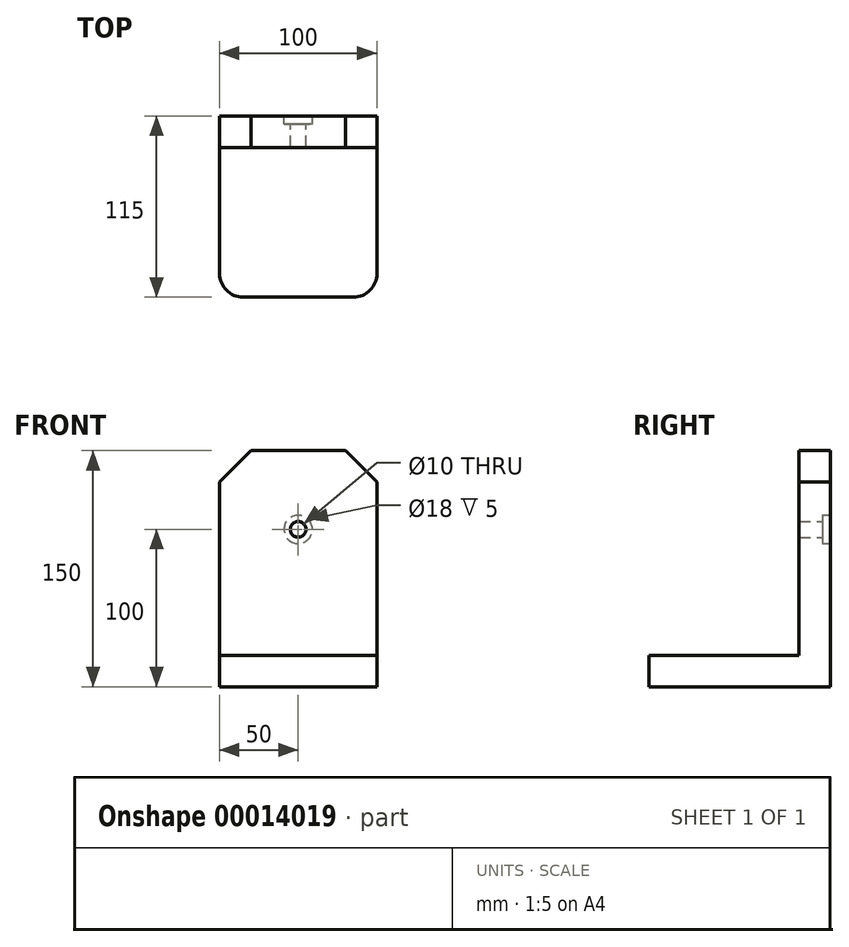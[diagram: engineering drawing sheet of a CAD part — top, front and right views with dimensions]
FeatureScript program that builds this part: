
annotation { "Feature Type Name" : "Feature", "Feature Type Description" : "" }
export const myFeature = defineFeature(function(context is Context, id is Id, definition is map)
    precondition{}
    {
        {
            var Q0;
            Q0=qCreatedBy(makeId("Right.planeOp"),FACE);
            var sketch = newSketch(context, id + "F0", { "sketchPlane" : qUnion([Q0])});
            skLineSegment(sketch, "E0.bottom", {"start": v(0, 0) * mm, "end": v(-20, 0) * mm});
            skLineSegment(sketch, "E0.top", {"start": v(0, 150) * mm, "end": v(-20, 150) * mm});
            skLineSegment(sketch, "E0.left", {"start": v(0, 0) * mm, "end": v(0, 150) * mm});
            skLineSegment(sketch, "E0.right", {"start": v(-20, 0) * mm, "end": v(-20, 150) * mm});
            skLineSegment(sketch, "E1.bottom", {"start": v(0, 20) * mm, "end": v(-115, 20) * mm});
            skLineSegment(sketch, "E1.top", {"start": v(0, 0) * mm, "end": v(-115, 0) * mm});
            skLineSegment(sketch, "E1.left", {"start": v(0, 20) * mm, "end": v(0, 0) * mm});
            skLineSegment(sketch, "E1.right", {"start": v(-115, 20) * mm, "end": v(-115, 0) * mm});
            skSolve(sketch);
        }
        {
            var Q0;
            Q0 = qSketchRegion(id + "F0", true);
            extrude(context, id + "F1", {"entities" : qUnion([Q0]), "endBound" : BoundingType.SYMMETRIC, "depth" : 100 * mm});
        }
        {
            var Q0;
            Q0=makeQuery(id+"F1.opExtrude","SWEPT_FACE",FACE,{"disambiguationData":[OSD([sQuery(id+"F0.wireOp",EDGE,"E0.left"),sQuery(id+"F0.wireOp",EDGE,"E1.left")])]});
            var sketch = newSketch(context, id + "F2", { "sketchPlane" : qUnion([Q0])});
            skPoint(sketch, "E2", {"position": v(0, 100) * mm});
            skSolve(sketch);
        }
        {
            var Q0;
            Q0=sQuery(id+"F2.wireOp",VERTEX,"E2");
            var Q1;
            Q1=makeQuery(id+"F1.opExtrude","SWEPT_BODY",BODY,{"disambiguationData":[OSD([sQuery(id+"F0.wireOp",EDGE,"E0.top"),sQuery(id+"F0.wireOp",EDGE,"E0.left"),sQuery(id+"F0.wireOp",EDGE,"E0.right"),sQuery(id+"F0.wireOp",EDGE,"E1.bottom"),sQuery(id+"F0.wireOp",EDGE,"E1.top"),sQuery(id+"F0.wireOp",EDGE,"E1.left"),sQuery(id+"F0.wireOp",EDGE,"E1.right")])]});
            hole(context, id + "F3", {"style" : HoleStyle.C_BORE, "holeDiameter" : 10 * mm, "cBoreDiameter" : 18 * mm, "cBoreDepth" : 5 * mm, "endStyle" : HoleEndStyle.THROUGH, "locations" : qUnion([Q0]), "scope" : qUnion([Q1])});
        }
        {
            var Q0;
            Q0=makeQuery(id+"F1.opExtrude","CAP_EDGE",EDGE,{"disambiguationData":[OSD([sQuery(id+"F0.wireOp",EDGE,"E1.right")])],"isStart":false});
            var Q1;
            Q1=makeQuery(id+"F1.opExtrude","CAP_EDGE",EDGE,{"disambiguationData":[OSD([sQuery(id+"F0.wireOp",EDGE,"E1.right")])],"isStart":true});
            fillet(context, id + "F4", {"entities" : qUnion([Q0, Q1]), "radius" : 15 * mm, "tangentPropagation" : true, "allowEdgeOverflow" : false});
        }
        {
            var Q0;
            Q0=makeQuery(id+"F1.opExtrude","CAP_EDGE",EDGE,{"disambiguationData":[OSD([sQuery(id+"F0.wireOp",EDGE,"E0.top")])],"isStart":true});
            var Q1;
            Q1=makeQuery(id+"F1.opExtrude","CAP_EDGE",EDGE,{"disambiguationData":[OSD([sQuery(id+"F0.wireOp",EDGE,"E0.top")])],"isStart":false});
            chamfer(context, id + "F5", {"entities" : qUnion([Q0, Q1]), "width" : 20 * mm, "tangentPropagation" : true});
        }
    });
